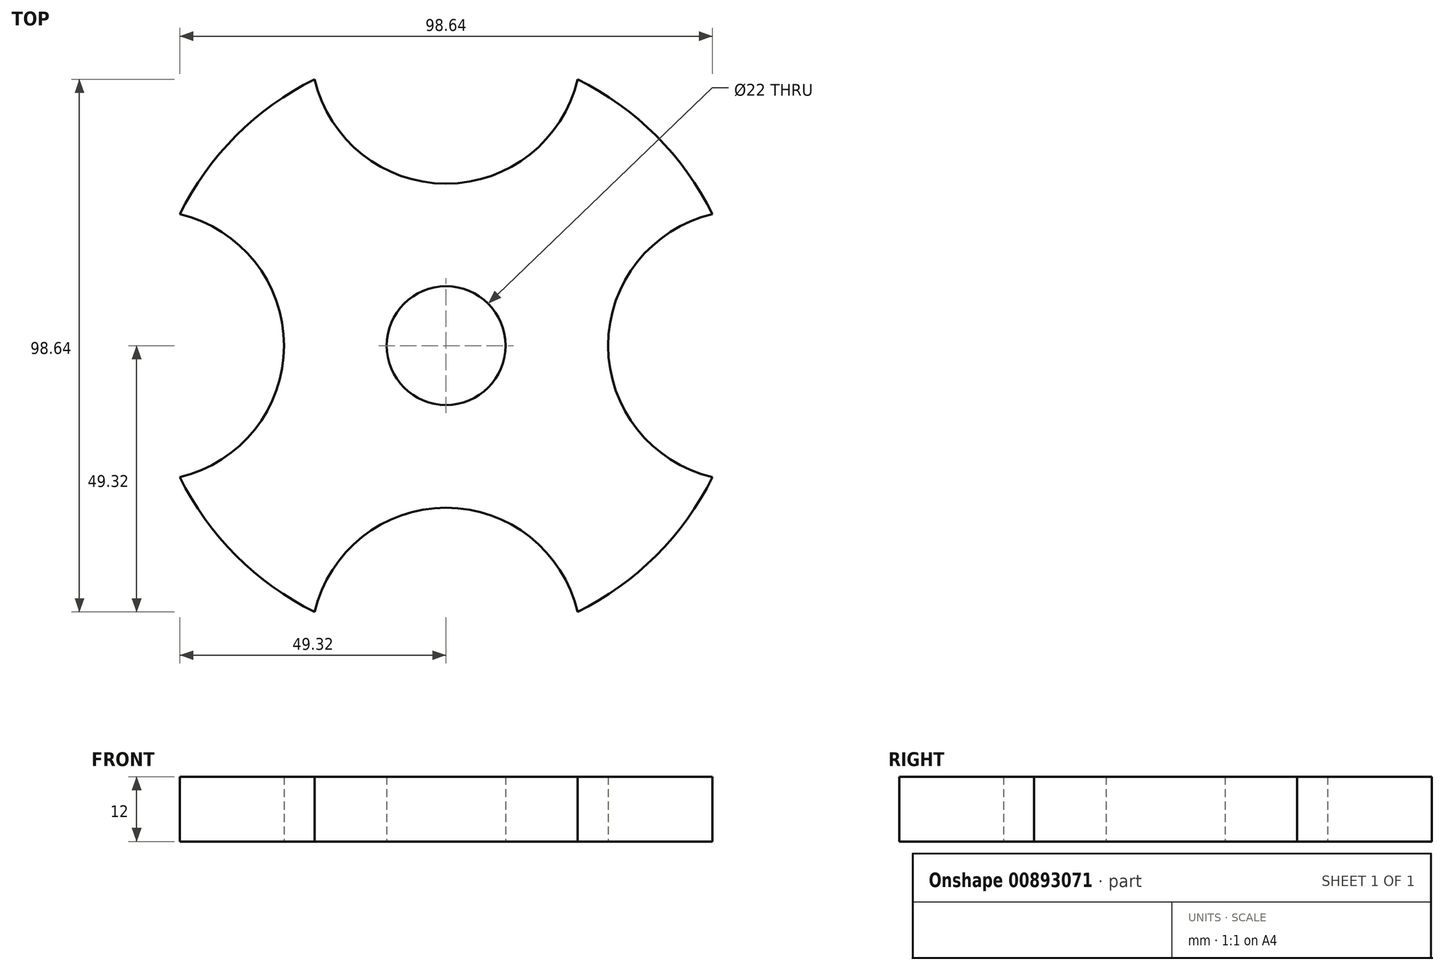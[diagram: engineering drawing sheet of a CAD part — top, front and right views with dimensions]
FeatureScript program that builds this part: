
annotation { "Feature Type Name" : "Feature", "Feature Type Description" : "" }
export const myFeature = defineFeature(function(context is Context, id is Id, definition is map)
    precondition{}
    {
        {
            var Q0;
            Q0=qCreatedBy(makeId("Top.planeOp"),FACE);
            var sketch = newSketch(context, id + "F0", { "sketchPlane" : qUnion([Q0])});
            skCircle(sketch, "E0", {"center": v(0, 0) * mm, "radius": 55 * mm});
            skCircle(sketch, "E1", {"center": v(0, 0) * mm, "radius": 11 * mm});
            skCircle(sketch, "E2", {"center": v(0, 55) * mm, "radius": 25 * mm});
            skCircle(sketch, "E3", {"center": v(55, 0) * mm, "radius": 25 * mm});
            skCircle(sketch, "E4", {"center": v(-55, 0) * mm, "radius": 25 * mm});
            skCircle(sketch, "E5", {"center": v(0, -55) * mm, "radius": 25 * mm});
            skSolve(sketch);
        }
        {
            var Q0;
            Q0=makeQuery(id+"F0.imprint","IMPRINT",FACE,{"disambiguationData":[TD([[makeQuery(id+"F0.imprint","IMPRINT",EDGE,{"derivedFrom":sQuery(id+"F0.wireOp",EDGE,"E1")}),-1.0]])]});
            extrude(context, id + "F1", {"entities" : qUnion([Q0]), "depth" : 12 * mm, "offsetDistance" : 25 * mm});
        }
    });
